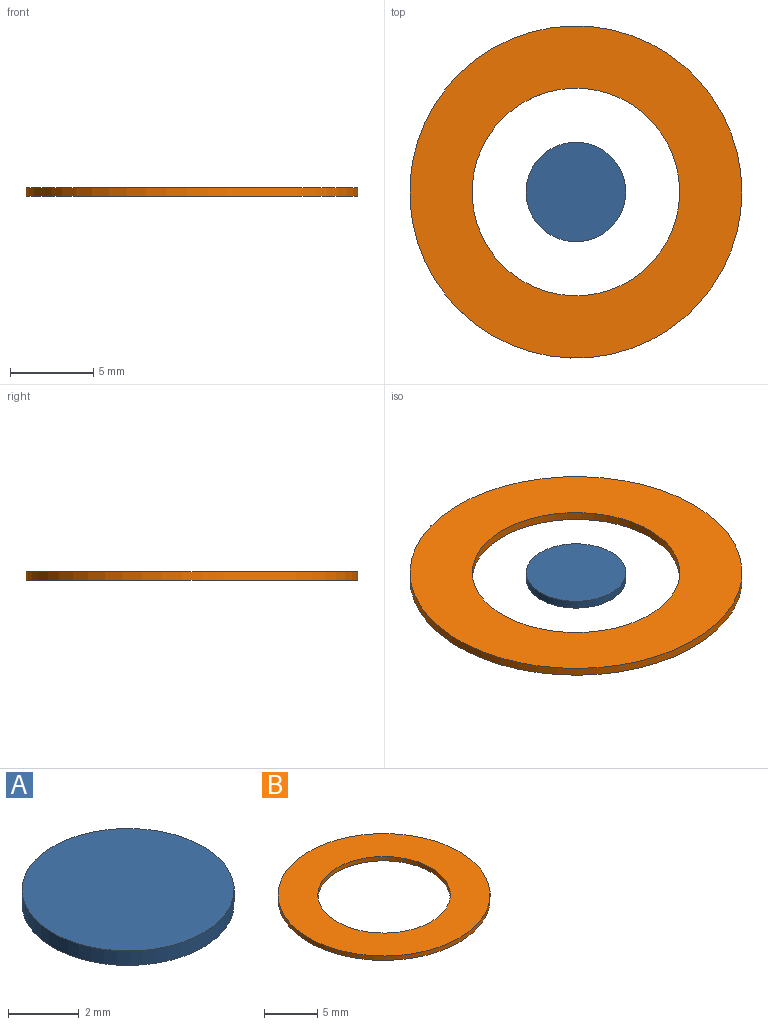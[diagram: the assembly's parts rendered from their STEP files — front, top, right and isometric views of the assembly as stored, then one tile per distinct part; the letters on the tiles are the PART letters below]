
ASSEMBLY  parts=2 mates=2
PART A: 3 faces, bbox 6x6x0.5 mm
  f0: cylinder r=3mm len=6mm, axis (0,0,-1), area 9.4mm2, adj f1,f2
  f1: plane 6x6mm, normal (0,0,1), area 28.3mm2, adj f0
  f2: plane 6x6mm, normal (0,0,-1), area 28.3mm2, adj f0
PART B: 4 faces, bbox 20x20x0.5 mm
  f0: cylinder r=6.25mm len=12.5mm, axis (0,0,-1), area 19.6mm2, adj f2,f3
  f1: cylinder r=10mm len=20mm, axis (0,0,-1), area 31.4mm2, adj f2,f3
  f2: plane 20x20mm, normal (0,0,1), area 191.4mm2, adj f0,f1
  f3: plane 20x20mm, normal (0,0,-1), area 191.4mm2, adj f0,f1
PLACE A t=(-2.88,2.34,-7.87)mm
PLACE B t=(-2.88,2.34,-7.87)mm
MATE planar B.f1 <-> A.f0  axis (0,0,1) through (-2.88,2.34,-7.37)mm
MATE parallel B.f1 <-> A.f0  axis (0,0,1) through (-2.88,2.34,-7.37)mm
